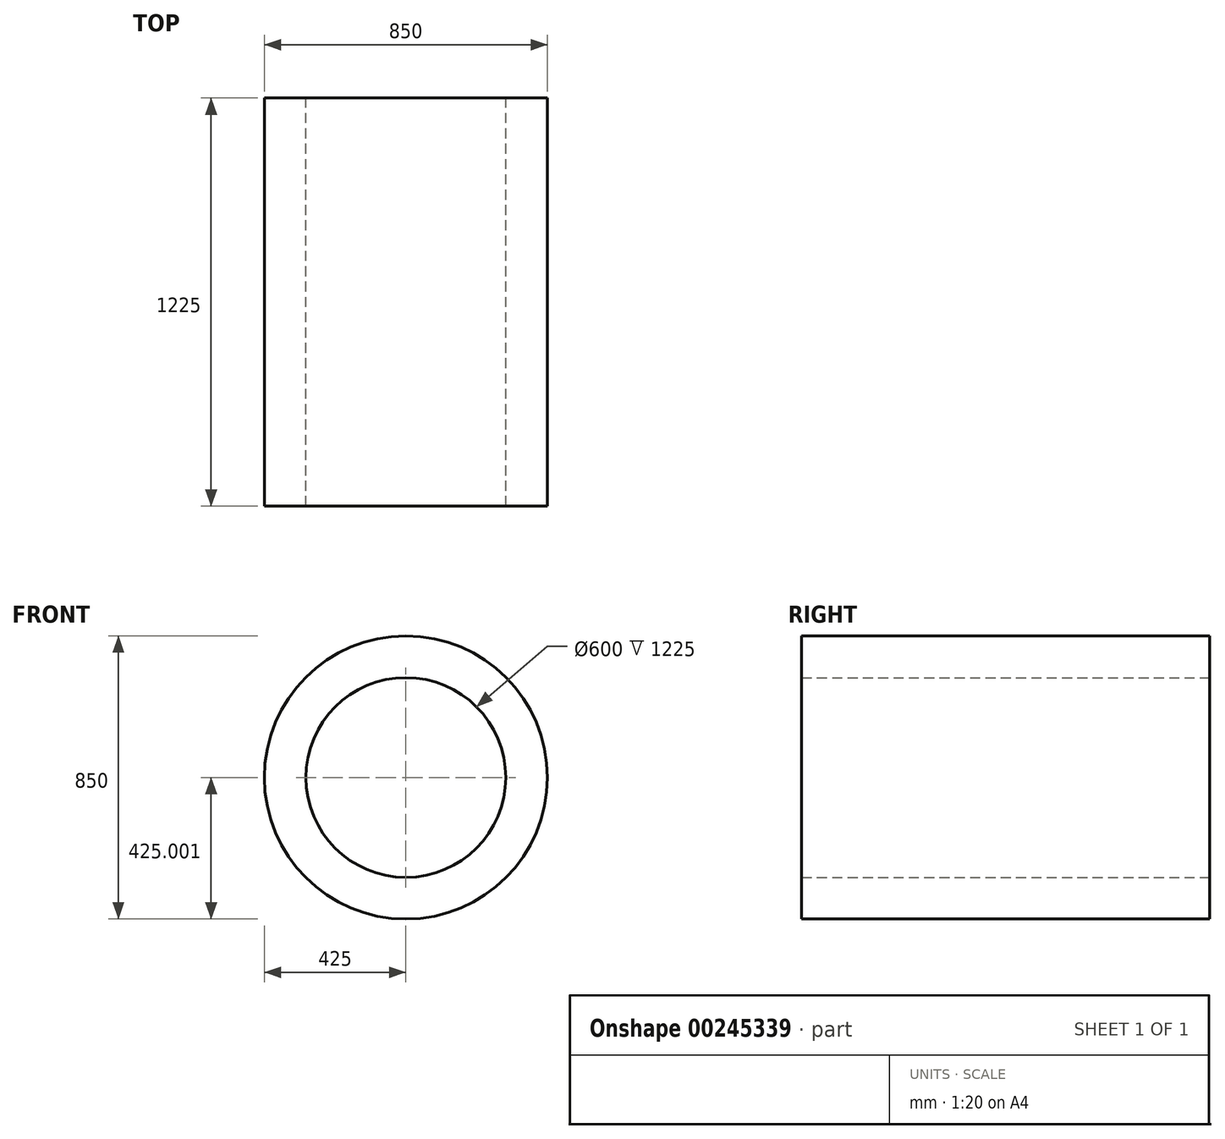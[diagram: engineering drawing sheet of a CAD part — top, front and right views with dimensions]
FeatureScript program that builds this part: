
annotation { "Feature Type Name" : "Feature", "Feature Type Description" : "" }
export const myFeature = defineFeature(function(context is Context, id is Id, definition is map)
    precondition{}
    {
        {
            var Q0;
            Q0=qCreatedBy(makeId("Front.planeOp"),FACE);
            var sketch = newSketch(context, id + "F0", { "sketchPlane" : qUnion([Q0])});
            skCircle(sketch, "E0", {"center": v(0, 601.04) * mm, "radius": 425 * mm});
            skLineSegment(sketch, "E1", {"start": v(0, 601.04) * mm, "end": v(835.68, 601.04) * mm, "construction": true});
            skLineSegment(sketch, "E2", {"start": v(835.68, 601.04) * mm, "end": v(0, 601.04) * mm, "construction": true});
            skLineSegment(sketch, "E3", {"start": v(-820.97, 601.04) * mm, "end": v(0, 601.04) * mm, "construction": true});
            skLineSegment(sketch, "E4", {"start": v(0, 0) * mm, "end": v(0, 1026.04) * mm, "construction": true});
            skLineSegment(sketch, "E5", {"start": v(-425, 176.04) * mm, "end": v(425, 1026.04) * mm, "construction": true});
            skLineSegment(sketch, "E6", {"start": v(-425, 1026.04) * mm, "end": v(425, 176.04) * mm, "construction": true});
            skLineSegment(sketch, "E7", {"start": v(0, 0) * mm, "end": v(-300.52, 300.52) * mm, "construction": true});
            skLineSegment(sketch, "E8", {"start": v(0, 0) * mm, "end": v(300.52, 300.52) * mm, "construction": true});
            skLineSegment(sketch, "E9", {"start": v(0, 0) * mm, "end": v(-601.04, 601.04) * mm});
            skLineSegment(sketch, "E10", {"start": v(0, 0) * mm, "end": v(601.04, 601.04) * mm});
            skCircle(sketch, "E11", {"center": v(0, 601.04) * mm, "radius": 300 * mm});
            skSolve(sketch);
        }
        {
            var Q0;
            Q0=makeQuery(id+"F0.imprint","IMPRINT",FACE,{"disambiguationData":[TD([[makeQuery(id+"F0.imprint","IMPRINT",EDGE,{"derivedFrom":sQuery(id+"F0.wireOp",EDGE,"E11")}),-1.0]])]});
            extrude(context, id + "F1", {"entities" : qUnion([Q0]), "depth" : 1225 * mm});
        }
    });
